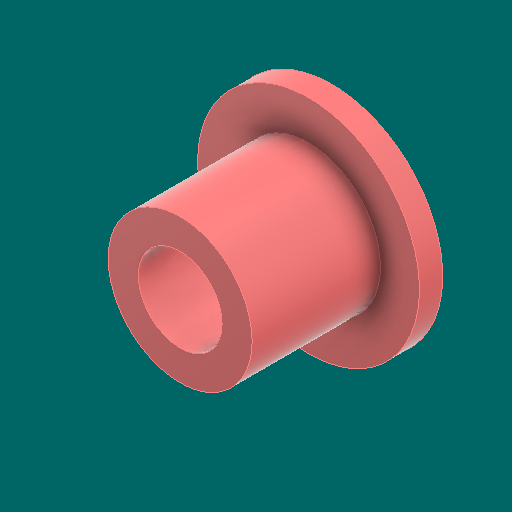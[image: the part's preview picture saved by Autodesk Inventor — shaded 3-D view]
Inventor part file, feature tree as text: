
AUTODESK INVENTOR PART (.ipt)
format: ipt  version: 2023.1 (Build 271208000, 208)  size: 138,240 bytes
history: native  units: in
note: dims shown in document units (in); Inventor stores cm internally (conversion verified against a paired STEP export)
features: other x3, sketch x2
ambient origin geometry x8: Origin, YZ Plane, XZ Plane, XY Plane, X Axis, Y Axis, Z Axis, Center Point
bodies: Solid1 (feature_tree)
feature tree (5):
  other  "bearingsleeve_MIR2.ipt"
  other  "Solid1::bearingsleeve_MIR2.ipt"
  other  "TaggingFeature1"
  sketch  "Sketch1"  dims[d0=0.3937in]
  sketch  "Sketch2"
